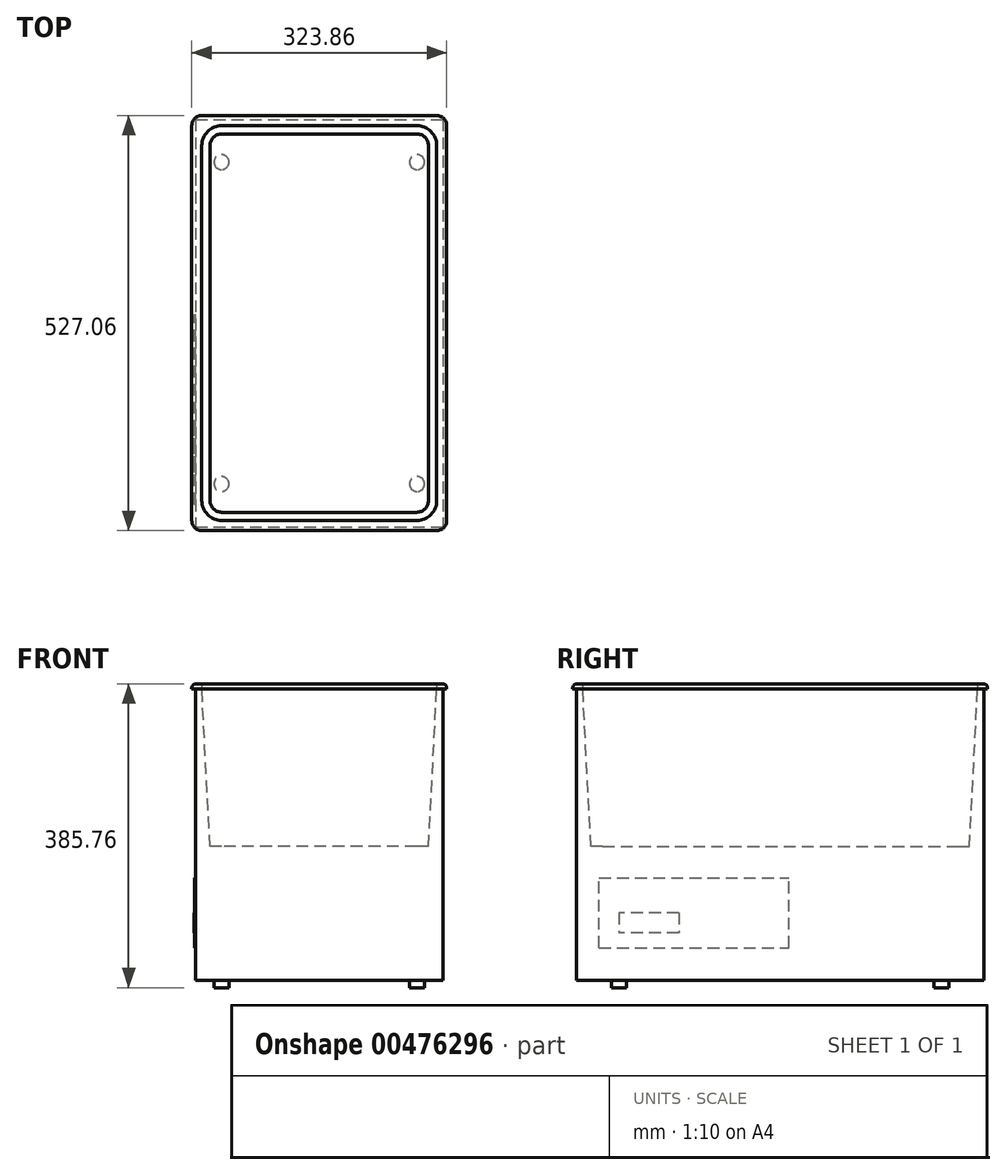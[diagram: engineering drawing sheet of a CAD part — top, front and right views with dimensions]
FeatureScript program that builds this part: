
annotation { "Feature Type Name" : "Feature", "Feature Type Description" : "" }
export const myFeature = defineFeature(function(context is Context, id is Id, definition is map)
    precondition{}
    {
        {
            var Q0;
            Q0=qCreatedBy(makeId("Top.planeOp"),FACE);
            var sketch = newSketch(context, id + "F0", { "sketchPlane" : qUnion([Q0])});
            skLineSegment(sketch, "E0.bottom", {"start": v(-157.16, 258.76) * mm, "end": v(157.16, 258.76) * mm});
            skLineSegment(sketch, "E0.top", {"start": v(-157.16, -258.76) * mm, "end": v(157.16, -258.76) * mm});
            skLineSegment(sketch, "E0.left", {"start": v(-157.16, 258.76) * mm, "end": v(-157.16, -258.76) * mm});
            skLineSegment(sketch, "E0.right", {"start": v(157.16, 258.76) * mm, "end": v(157.16, -258.76) * mm});
            skLineSegment(sketch, "E1", {"start": v(-157.16, 258.76) * mm, "end": v(157.16, -258.76) * mm, "construction": true});
            skPoint(sketch, "E2", {"position": v(0, 0) * mm});
            skSolve(sketch);
        }
        {
            var Q0;
            Q0 = qSketchRegion(id + "F0", true);
            extrude(context, id + "F1", {"entities" : qUnion([Q0]), "oppositeDirection" : true, "depth" : 369.9 * mm, "offsetDistance" : 25.4 * mm});
        }
        {
            var Q0;
            Q0=makeQuery(id+"F1.opExtrude","CAP_FACE",FACE,{"disambiguationData":[OSD([sQuery(id+"F0.wireOp",EDGE,"E0.bottom"),sQuery(id+"F0.wireOp",EDGE,"E0.top"),sQuery(id+"F0.wireOp",EDGE,"E0.left"),sQuery(id+"F0.wireOp",EDGE,"E0.right")])],"isStart":true});
            var sketch = newSketch(context, id + "F2", { "sketchPlane" : qUnion([Q0])});
            skLineSegment(sketch, "E3.bottom", {"start": v(-123.82, 250.82) * mm, "end": v(123.82, 250.82) * mm});
            skLineSegment(sketch, "E3.top", {"start": v(-123.82, -250.83) * mm, "end": v(123.82, -250.83) * mm});
            skLineSegment(sketch, "E3.left", {"start": v(-149.22, 225.42) * mm, "end": v(-149.23, -225.42) * mm});
            skLineSegment(sketch, "E3.right", {"start": v(149.23, 225.42) * mm, "end": v(149.23, -225.42) * mm});
            skLineSegment(sketch, "E4", {"start": v(149.23, 250.83) * mm, "end": v(-149.23, -250.83) * mm, "construction": true});
            skPoint(sketch, "E5", {"position": v(0, 0) * mm});
            skPoint(sketch, "E6.visualSharp", {"position": v(-149.22, 250.82) * mm});
            skArc(sketch, "E6.filletArc", {"start": v(-123.82, 250.82) * mm, "mid": v(-141.79, 243.39) * mm, "end": v(-149.22, 225.42) * mm});
            skPoint(sketch, "E7.visualSharp", {"position": v(149.23, 250.82) * mm});
            skArc(sketch, "E7.filletArc", {"start": v(149.23, 225.42) * mm, "mid": v(141.79, 243.39) * mm, "end": v(123.82, 250.82) * mm});
            skPoint(sketch, "E8.visualSharp", {"position": v(149.22, -250.83) * mm});
            skArc(sketch, "E8.filletArc", {"start": v(123.82, -250.83) * mm, "mid": v(141.79, -243.39) * mm, "end": v(149.22, -225.42) * mm});
            skPoint(sketch, "E9.visualSharp", {"position": v(-149.23, -250.83) * mm});
            skArc(sketch, "E9.filletArc", {"start": v(-149.23, -225.42) * mm, "mid": v(-141.79, -243.39) * mm, "end": v(-123.82, -250.83) * mm});
            skSolve(sketch);
        }
        {
            var Q0;
            Q0 = qSketchRegion(id + "F2", true);
            extrude(context, id + "F3", {"entities" : qUnion([Q0]), "operationType" : NewBodyOperationType.REMOVE, "oppositeDirection" : true, "depth" : 200.02 * mm, "offsetDistance" : 25.4 * mm, "hasDraft" : true, "draftAngle" : 3 * degree, "draftPullDirection" : true});
        }
        {
            var Q0;
            Q0=makeQuery(id+"F1.opExtrude","CAP_FACE",FACE,{"disambiguationData":[OSD([sQuery(id+"F0.wireOp",EDGE,"E0.bottom"),sQuery(id+"F0.wireOp",EDGE,"E0.top"),sQuery(id+"F0.wireOp",EDGE,"E0.left"),sQuery(id+"F0.wireOp",EDGE,"E0.right")])],"isStart":false});
            var sketch = newSketch(context, id + "F4", { "sketchPlane" : qUnion([Q0])});
            skLineSegment(sketch, "E10", {"start": v(-157.16, 258.76) * mm, "end": v(157.16, -258.76) * mm, "construction": true});
            skLineSegment(sketch, "E11", {"start": v(157.16, 258.76) * mm, "end": v(-157.16, -258.76) * mm, "construction": true});
            skCircle(sketch, "E12", {"center": v(-124.2, 204.49) * mm, "radius": 9.52 * mm});
            skCircle(sketch, "E13", {"center": v(124.2, 204.49) * mm, "radius": 9.52 * mm});
            skCircle(sketch, "E14", {"center": v(124.2, -204.49) * mm, "radius": 9.52 * mm});
            skCircle(sketch, "E15", {"center": v(-124.2, -204.49) * mm, "radius": 9.52 * mm});
            skSolve(sketch);
        }
        {
            var Q0;
            Q0 = qSketchRegion(id + "F4", true);
            extrude(context, id + "F5", {"entities" : qUnion([Q0]), "operationType" : NewBodyOperationType.ADD, "depth" : 9.52 * mm, "offsetDistance" : 25.4 * mm});
        }
        {
            var Q0;
            Q0=makeQuery(id+"F1.opExtrude","CAP_FACE",FACE,{"disambiguationData":[OSD([sQuery(id+"F0.wireOp",EDGE,"E0.bottom"),sQuery(id+"F0.wireOp",EDGE,"E0.top"),sQuery(id+"F0.wireOp",EDGE,"E0.left"),sQuery(id+"F0.wireOp",EDGE,"E0.right")])],"isStart":true});
            var sketch = newSketch(context, id + "F6", { "sketchPlane" : qUnion([Q0])});
            skLineSegment(sketch, "E16.bottom", {"start": v(-123.82, 250.82) * mm, "end": v(123.82, 250.82) * mm});
            skLineSegment(sketch, "E16.top", {"start": v(-123.82, -250.83) * mm, "end": v(123.82, -250.83) * mm});
            skLineSegment(sketch, "E16.left", {"start": v(-149.23, 225.42) * mm, "end": v(-149.22, -225.42) * mm});
            skLineSegment(sketch, "E16.right", {"start": v(149.23, 225.42) * mm, "end": v(149.23, -225.42) * mm});
            skPoint(sketch, "E17.visualSharp", {"position": v(-149.23, 250.82) * mm});
            skArc(sketch, "E17.filletArc", {"start": v(-123.82, 250.82) * mm, "mid": v(-141.79, 243.39) * mm, "end": v(-149.23, 225.42) * mm});
            skPoint(sketch, "E18.visualSharp", {"position": v(149.23, 250.82) * mm});
            skArc(sketch, "E18.filletArc", {"start": v(149.23, 225.42) * mm, "mid": v(141.79, 243.39) * mm, "end": v(123.82, 250.82) * mm});
            skPoint(sketch, "E19.visualSharp", {"position": v(149.23, -250.83) * mm});
            skArc(sketch, "E19.filletArc", {"start": v(123.82, -250.83) * mm, "mid": v(141.79, -243.39) * mm, "end": v(149.23, -225.42) * mm});
            skPoint(sketch, "E20.visualSharp", {"position": v(-149.22, -250.83) * mm});
            skArc(sketch, "E20.filletArc", {"start": v(-149.22, -225.42) * mm, "mid": v(-141.79, -243.39) * mm, "end": v(-123.82, -250.83) * mm});
            skLineSegment(sketch, "E21.bottom", {"start": v(-149.23, 263.52) * mm, "end": v(149.23, 263.52) * mm});
            skLineSegment(sketch, "E21.top", {"start": v(-149.22, -263.53) * mm, "end": v(149.23, -263.53) * mm});
            skLineSegment(sketch, "E21.left", {"start": v(-161.93, 250.82) * mm, "end": v(-161.92, -250.83) * mm});
            skLineSegment(sketch, "E21.right", {"start": v(161.93, 250.82) * mm, "end": v(161.93, -250.83) * mm});
            skPoint(sketch, "E22.visualSharp", {"position": v(-161.93, 263.52) * mm});
            skArc(sketch, "E22.filletArc", {"start": v(-149.23, 263.52) * mm, "mid": v(-158.2, 259.8) * mm, "end": v(-161.93, 250.82) * mm});
            skPoint(sketch, "E23.visualSharp", {"position": v(161.93, 263.52) * mm});
            skArc(sketch, "E23.filletArc", {"start": v(161.93, 250.82) * mm, "mid": v(158.2, 259.8) * mm, "end": v(149.23, 263.52) * mm});
            skPoint(sketch, "E24.visualSharp", {"position": v(161.93, -263.53) * mm});
            skArc(sketch, "E24.filletArc", {"start": v(149.23, -263.53) * mm, "mid": v(158.2, -259.8) * mm, "end": v(161.93, -250.83) * mm});
            skPoint(sketch, "E25.visualSharp", {"position": v(-161.92, -263.53) * mm});
            skArc(sketch, "E25.filletArc", {"start": v(-161.92, -250.83) * mm, "mid": v(-158.2, -259.8) * mm, "end": v(-149.22, -263.53) * mm});
            skSolve(sketch);
        }
        {
            var Q0;
            Q0 = qSketchRegion(id + "F6", true);
            extrude(context, id + "F7", {"entities" : qUnion([Q0]), "operationType" : NewBodyOperationType.ADD, "depth" : 6.35 * mm, "offsetDistance" : 25.4 * mm});
        }
        {
            var Q0;
            Q0=makeQuery(id+"F7.opExtrude","CAP_EDGE",EDGE,{"disambiguationData":[OSD([sQuery(id+"F6.wireOp",EDGE,"E21.right")])],"isStart":false});
            fillet(context, id + "F8", {"entities" : qUnion([Q0]), "radius" : 5.08 * mm, "tangentPropagation" : true, "allowEdgeOverflow" : false});
        }
        {
            var Q0;
            Q0=makeQuery(id+"F1.opExtrude","SWEPT_FACE",FACE,{"disambiguationData":[OSD([sQuery(id+"F0.wireOp",EDGE,"E0.left")])]});
            var sketch = newSketch(context, id + "F9", { "sketchPlane" : qUnion([Q0])});
            skLineSegment(sketch, "E26.bottom", {"start": v(230.19, -328.61) * mm, "end": v(-11.11, -328.61) * mm});
            skLineSegment(sketch, "E26.top", {"start": v(230.19, -239.71) * mm, "end": v(-11.11, -239.71) * mm});
            skLineSegment(sketch, "E26.left", {"start": v(230.19, -328.61) * mm, "end": v(230.19, -239.71) * mm});
            skLineSegment(sketch, "E26.right", {"start": v(-11.11, -328.61) * mm, "end": v(-11.11, -239.71) * mm});
            skSolve(sketch);
        }
        {
            var Q0;
            Q0 = qSketchRegion(id + "F9", true);
            extrude(context, id + "F10", {"entities" : qUnion([Q0]), "operationType" : NewBodyOperationType.ADD, "depth" : 1.27 * mm, "offsetDistance" : 25.4 * mm});
        }
        {
            var Q0;
            Q0=makeQuery(id+"F10.opExtrude","CAP_FACE",FACE,{"disambiguationData":[OSD([sQuery(id+"F9.wireOp",EDGE,"E26.bottom"),sQuery(id+"F9.wireOp",EDGE,"E26.top"),sQuery(id+"F9.wireOp",EDGE,"E26.left"),sQuery(id+"F9.wireOp",EDGE,"E26.right")])],"isStart":false});
            var sketch = newSketch(context, id + "F11", { "sketchPlane" : qUnion([Q0])});
            skLineSegment(sketch, "E27.bottom", {"start": v(128.59, -284.16) * mm, "end": v(204.79, -284.16) * mm});
            skLineSegment(sketch, "E27.top", {"start": v(128.59, -309.56) * mm, "end": v(204.79, -309.56) * mm});
            skLineSegment(sketch, "E27.left", {"start": v(128.59, -284.16) * mm, "end": v(128.59, -309.56) * mm});
            skLineSegment(sketch, "E27.right", {"start": v(204.79, -284.16) * mm, "end": v(204.79, -309.56) * mm});
            skLineSegment(sketch, "E28", {"start": v(153.99, -284.16) * mm, "end": v(153.99, -309.56) * mm});
            skLineSegment(sketch, "E29", {"start": v(166.69, -284.16) * mm, "end": v(166.69, -309.56) * mm});
            skLineSegment(sketch, "E30", {"start": v(179.39, -284.16) * mm, "end": v(179.39, -309.56) * mm});
            skSolve(sketch);
        }
        {
            var Q0;
            Q0 = qSketchRegion(id + "F11", true);
            extrude(context, id + "F12", {"entities" : qUnion([Q0]), "operationType" : NewBodyOperationType.ADD, "depth" : 0.76 * mm, "offsetDistance" : 25.4 * mm});
        }
    });
